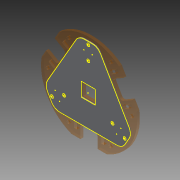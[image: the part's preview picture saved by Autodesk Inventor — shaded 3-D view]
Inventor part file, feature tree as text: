
AUTODESK INVENTOR PART (.ipt)
format: ipt  version: 2015 (Build 190159000, 159)  size: 393,216 bytes
history: native  units: mm
features: other x4, sketch x2, projected_geometry x2, extrude x1
ambient origin geometry x8: Origin, YZ Plane, XZ Plane, XY Plane, X Axis, Y Axis, Z Axis, Center Point
bodies: Solid1 (feature_tree)
feature tree (9):
  other  "top plate.ipt"
  extrude  "Extrusion1"  Depth=1.0mm
  sketch  "Sketch2"  dims[d2=1.0mm d3=3.2mm d7=3.0mm d8=3.2mm d9=120.0deg d10=120.0deg d11=3.0mm d12=3.0mm d13=3.2mm d14=3.2mm d15=3.2mm d16=3.2mm d17=10.0mm d18=10.0mm d19=1.0mm d20=0.0mm]
  other  "TaggingFeature1"
  sketch  "Sketch1"  dims[d0=10.0mm d1=1.0mm]
  projected_geometry  "Projected Loop1"
  other  "Solid1::top plate.ipt"
  other  "Srf1"
  projected_geometry  "Project Cut Edges1"
